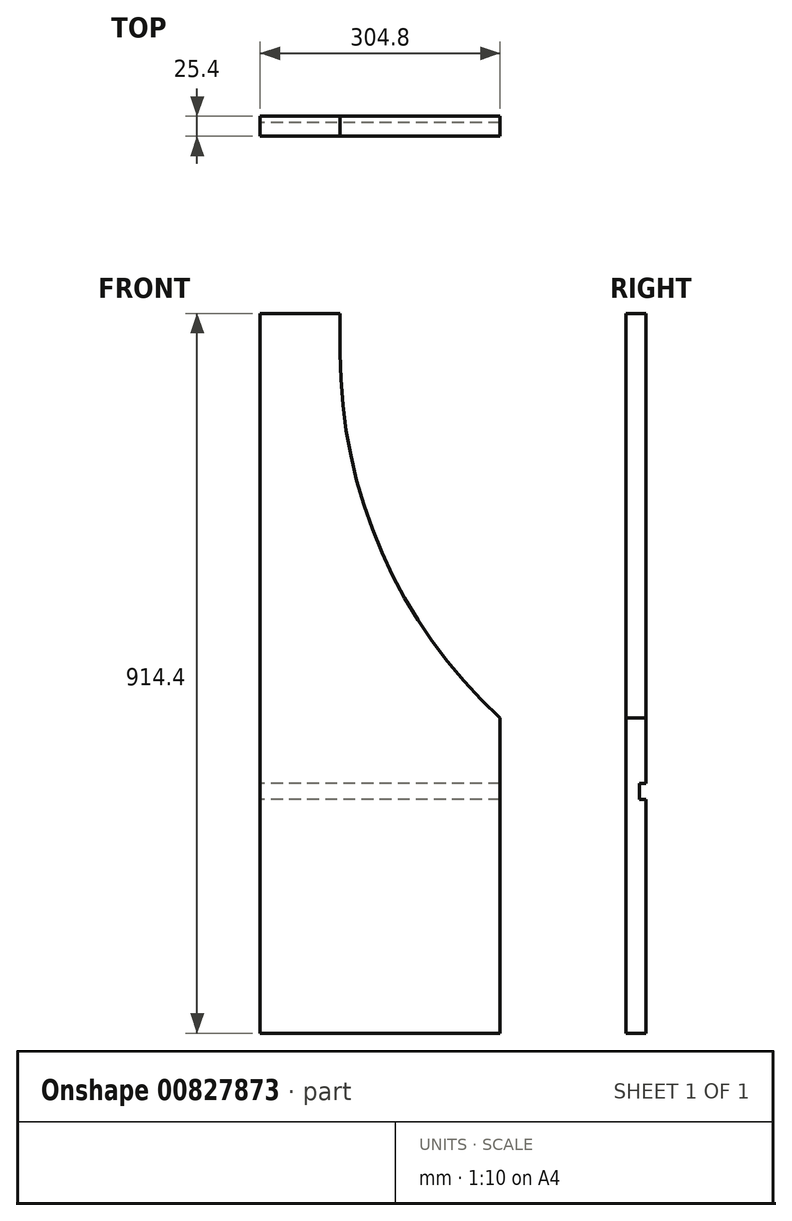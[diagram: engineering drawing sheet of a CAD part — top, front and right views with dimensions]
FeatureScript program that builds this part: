
annotation { "Feature Type Name" : "Feature", "Feature Type Description" : "" }
export const myFeature = defineFeature(function(context is Context, id is Id, definition is map)
    precondition{}
    {
        {
            var Q0;
            Q0=qCreatedBy(makeId("Front.planeOp"),FACE);
            var sketch = newSketch(context, id + "F0", { "sketchPlane" : qUnion([Q0])});
            skLineSegment(sketch, "E0", {"start": v(203.2, -1180.33) * mm, "end": v(203.2, -1497.83) * mm});
            skLineSegment(sketch, "E1", {"start": v(203.2, -1497.83) * mm, "end": v(-101.6, -1497.83) * mm});
            skLineSegment(sketch, "E2", {"start": v(-101.6, -1497.83) * mm, "end": v(-101.6, -583.43) * mm});
            skLineSegment(sketch, "E3", {"start": v(-101.6, -583.43) * mm, "end": v(0, -583.43) * mm});
            skLineSegment(sketch, "E4", {"start": v(0, -583.43) * mm, "end": v(0, -634.23) * mm});
            skArc(sketch, "E5", {"start": v(0, -634.23) * mm, "mid": v(53.03, -887.18) * mm, "end": v(203.2, -1097.52) * mm});
            skLineSegment(sketch, "E6", {"start": v(203.2, -1180.33) * mm, "end": v(203.2, -1097.52) * mm});
            skLineSegment(sketch, "E7.bottom", {"start": v(203.2, -1180.33) * mm, "end": v(-101.6, -1180.33) * mm});
            skLineSegment(sketch, "E7.top", {"start": v(203.2, -1200.65) * mm, "end": v(-101.6, -1200.65) * mm});
            skLineSegment(sketch, "E7.left", {"start": v(203.2, -1180.33) * mm, "end": v(203.2, -1200.65) * mm});
            skLineSegment(sketch, "E7.right", {"start": v(-101.6, -1180.33) * mm, "end": v(-101.6, -1200.65) * mm});
            skSolve(sketch);
        }
        {
            var Q0;
            Q0 = qSketchRegion(id + "F0", true);
            extrude(context, id + "F1", {"entities" : qUnion([Q0]), "depth" : 25.4 * mm, "offsetDistance" : 25.4 * mm});
        }
        {
            var Q0;
            Q0=makeQuery(id+"F0.imprint","IMPRINT",FACE,{"disambiguationData":[TD([[makeQuery(id+"F0.imprint","IMPRINT",EDGE,{"derivedFrom":sQuery(id+"F0.wireOp",EDGE,"E7.bottom")}),1.0]])]});
            extrude(context, id + "F2", {"entities" : qUnion([Q0]), "operationType" : NewBodyOperationType.REMOVE, "depth" : 8.25 * mm, "offsetDistance" : 25.4 * mm});
        }
    });
